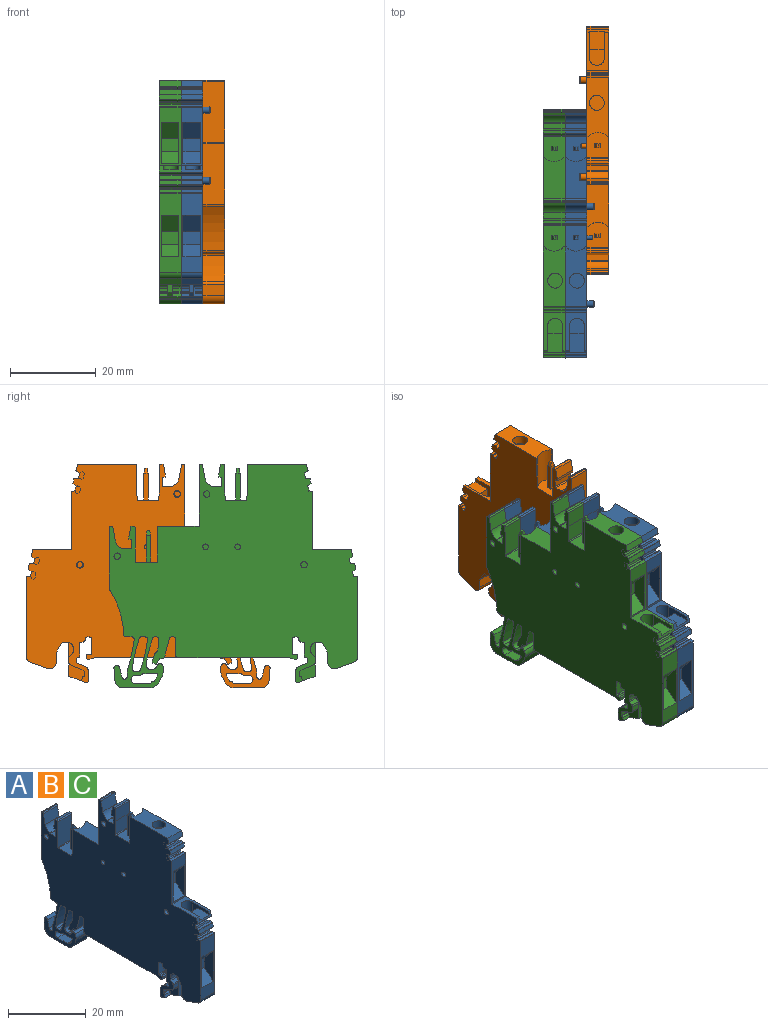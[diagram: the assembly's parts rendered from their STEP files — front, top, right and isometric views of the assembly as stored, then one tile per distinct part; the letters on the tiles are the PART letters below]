
ASSEMBLY  parts=3 mates=3
PART A: 301 faces, bbox 6.8x58x52.3 mm
  f0: cylinder r=0.8mm len=1.6mm, axis (-1,0,0), area 7.6mm2, adj f1,f34
  f1: cone r=0.8mm half-angle=30deg, axis (-1,0,0), area 1.1mm2, adj f0,f287
  f2: plane 1.49x1.49mm, normal (-1,0,0), area 1.7mm2, adj f277
  f3: plane 4.3x0.22mm, normal (0,1,0.02), area 0.8mm2, adj f6,f7,f35,f279
  f4: plane 4.1x0.3mm, normal (0,1,0), area 1.2mm2, adj f5,f34,f56,f279
  f5: plane 4.3x0.3mm, normal (0,1,0.02), area 1.2mm2, adj f4,f7,f34,f279
  f6: plane 4.1x0.22mm, normal (0,1,0), area 0.9mm2, adj f3,f35,f56,f279
  f7: plane 5.93x5.08mm, normal (0,0,1), area 27mm2, adj f3,f5,f34,f35,f229,f258,f259,f260
  f8: cylinder r=1.74mm len=3.48mm, axis (0,0,1), area 23.5mm2, adj f9,f33
  f9: plane 13.79x5.08mm, normal (0,0,1), area 57.6mm2, adj f8,f10,f12,f34,f35,f278,f290
  f10: plane 5.08x1.54mm, normal (0,-0.97,0.24), area 8.1mm2, adj f9,f34,f35,f113
  f11: plane 5.93x5.08mm, normal (0,0,1), area 27mm2, adj f13,f14,f34,f35,f249,f250,f251,f252
  f12: plane 4.1x0.22mm, normal (0,1,0), area 0.9mm2, adj f9,f13,f35,f278
  f13: plane 4.3x0.22mm, normal (0,1,0.02), area 0.8mm2, adj f11,f12,f35,f278
  f14: cylinder r=0.2mm len=5.08mm, axis (1,0,0), area 1.6mm2, adj f11,f15,f34,f35
  f15: plane 5.08x4.1mm, normal (0,-1,0.02), area 20.8mm2, adj f14,f16,f34,f35
  f16: plane 5.08x3.8mm, normal (0,-1,0), area 19.3mm2, adj f15,f17,f34,f35
  f17: cylinder r=0.3mm len=5.08mm, axis (1,0,0), area 2.4mm2, adj f16,f18,f34,f35
  f18: plane 5.08x0.68mm, normal (0,0,1), area 3.5mm2, adj f17,f19,f34,f35
  f19: plane 5.08x2.5mm, normal (0,0.98,0.17), area 12.9mm2, adj f18,f20,f34,f35
  f20: plane 5.08x0.6mm, normal (0,1,0), area 3mm2, adj f19,f21,f34,f35
  f21: plane 5.08x0.67mm, normal (0,0,-1), area 3.4mm2, adj f20,f22,f34,f35
  f22: plane 5.08x1.95mm, normal (0,1,0), area 9.9mm2, adj f21,f23,f34,f35
  f23: cylinder r=0.25mm len=5.08mm, axis (1,0,0), area 2mm2, adj f22,f24,f34,f35
  f24: plane 5.08x1.72mm, normal (0,0,1), area 8.8mm2, adj f23,f25,f34,f35
  f25: cylinder r=0.5mm len=5.08mm, axis (1,0,0), area 0.8mm2, adj f24,f26,f34,f35
  f26: cylinder r=2.57mm len=5.08mm, axis (1,0,0), area 13.5mm2, adj f25,f27,f34,f35
  f27: plane 5.08x3.17mm, normal (0,-0.98,0.18), area 16.3mm2, adj f26,f28,f34,f35
  f28: cylinder r=0.3mm len=5.08mm, axis (1,0,0), area 2.1mm2, adj f27,f29,f34,f35
  f29: plane 5.08x0.24mm, normal (0,0,1), area 1.2mm2, adj f28,f30,f34,f35
  f30: cylinder r=0.3mm len=5.08mm, axis (1,0,0), area 2.4mm2, adj f29,f34,f35,f55
  f31: cylinder r=1.74mm len=3.9mm, axis (0,0,1), area 21.3mm2, adj f32,f65,f66,f68
  f32: plane 6.13x3.9mm, normal (1,0,0), area 11.5mm2, adj f31,f64,f65,f67,f68,f90
  f33: plane 3.48x3.48mm, normal (0,0,1), area 9.5mm2, adj f8
  f34: plane 58x52.25mm, normal (1,0,0), area 1913mm2, adj f0,f4,f5,f7,f9,f10,f11,f14
  f35: plane 58x52.25mm, normal (-1,0,0), area 1919.5mm2, adj f3,f6,f7,f9,f10,f11,f12,f13
  f36: cylinder r=0.5mm len=5.08mm, axis (1,0,0), area 3mm2, adj f34,f35,f37,f43
  f37: cylinder r=35mm len=7.13mm, axis (1,0,0), area 37.2mm2, adj f34,f35,f36,f38
  f38: cylinder r=0.5mm len=5.08mm, axis (1,0,0), area 4.3mm2, adj f34,f35,f37,f39
  f39: plane 5.08x0.99mm, normal (0,0,1), area 5mm2, adj f34,f35,f38,f40
  f40: cylinder r=0.5mm len=5.08mm, axis (1,0,0), area 3.2mm2, adj f34,f35,f39,f41
  f41: cylinder r=35mm len=7.1mm, axis (1,0,0), area 37mm2, adj f34,f35,f40,f42
  f42: cylinder r=0.5mm len=5.08mm, axis (1,0,0), area 4.3mm2, adj f34,f35,f41,f43
  f43: plane 5.08x0.97mm, normal (0,0,-1), area 4.9mm2, adj f34,f35,f36,f42
  f44: plane 5.08x3.02mm, normal (0,0,-1), area 15.4mm2, adj f34,f35,f45,f54
  f45: cylinder r=0.5mm len=5.08mm, axis (1,0,0), area 1.7mm2, adj f34,f35,f44,f46
  f46: cylinder r=1.5mm len=5.08mm, axis (1,0,0), area 5.1mm2, adj f34,f35,f45,f47
  f47: plane 5.08x0.83mm, normal (0,0,-1), area 4.2mm2, adj f34,f35,f46,f48
  f48: cylinder r=0.95mm len=5.08mm, axis (1,0,0), area 15.2mm2, adj f34,f35,f47,f49
  f49: plane 5.08x3.47mm, normal (0,0,1), area 17.6mm2, adj f34,f35,f48,f50
  f50: cylinder r=0.25mm len=5.08mm, axis (1,0,0), area 1.5mm2, adj f34,f35,f49,f51
  f51: cylinder r=0.65mm len=5.08mm, axis (1,0,0), area 4.2mm2, adj f34,f35,f50,f52
  f52: cylinder r=0.25mm len=5.08mm, axis (1,0,0), area 1.4mm2, adj f34,f35,f51,f53
  f53: cylinder r=8.5mm len=5.08mm, axis (1,0,0), area 7.6mm2, adj f34,f35,f52,f54
  f54: cylinder r=0.25mm len=5.08mm, axis (1,0,0), area 2.5mm2, adj f34,f35,f44,f53
  f55: plane 14.2x5.08mm, normal (0,1,0), area 72.1mm2, adj f30,f34,f35,f56
  f56: plane 9.68x5.08mm, normal (0,0,1), area 46.2mm2, adj f4,f6,f34,f35,f55,f279
  f57: plane 1.84x1.31mm, normal (1,0,0), area 1.7mm2, adj f58,f93,f94,f95,f96,f97,f98,f99
  f58: plane 1.24x0.31mm, normal (0,-0.97,0.24), area 0.2mm2, adj f35,f57,f93,f99
  f59: plane 1.24x0.31mm, normal (0,-0.97,0.24), area 0.2mm2, adj f35,f63,f81,f87
  f60: plane 1.73x1.41mm, normal (1,0,0), area 1.7mm2, adj f61,f105,f106,f107,f108,f109,f110,f111
  f61: plane 1.24x0.31mm, normal (0,-0.97,0.24), area 0.2mm2, adj f35,f60,f105,f111
  f62: plane 2.91x1.06mm, normal (0,-0.34,-0.94), area 3.1mm2, adj f136,f235,f236,f237
  f63: plane 1.73x1.41mm, normal (1,0,0), area 1.7mm2, adj f59,f81,f82,f83,f84,f85,f86,f87
  f64: plane 4.23x3.48mm, normal (0,0,1), area 14.7mm2, adj f32,f66,f67,f90
  f65: plane 3.64x3.48mm, normal (0,0,1), area 11.4mm2, adj f31,f32,f66,f67
  f66: plane 6.13x3.9mm, normal (-1,0,0), area 11.5mm2, adj f31,f64,f65,f67,f68,f90
  f67: plane 3.48x2.9mm, normal (0,1,0), area 10.1mm2, adj f32,f64,f65,f66
  f68: plane 8.9x5.08mm, normal (0,0,1), area 20mm2, adj f31,f32,f34,f35,f66,f90,f91
  f69: plane 5.08x0.19mm, normal (0,0.24,0.97), area 1mm2, adj f34,f35,f71,f114,f299,f300
  f70: plane 5.08x0.92mm, normal (0,-0.24,-0.97), area 4.7mm2, adj f34,f35,f75,f76,f299,f300
  f71: plane 4.96x0.52mm, normal (0,0.86,0.51), area 3mm2, adj f34,f69,f72,f299
  f72: plane 4.96x0.32mm, normal (0,0.24,0.97), area 1.6mm2, adj f34,f71,f73,f299
  f73: plane 4.96x0.36mm, normal (0,-0.51,0.86), area 2.1mm2, adj f34,f72,f74,f299
  f74: plane 4.96x1.07mm, normal (0,-0.97,0.24), area 5.5mm2, adj f34,f73,f75,f299
  f75: plane 4.96x0.36mm, normal (0,-0.86,-0.51), area 2.1mm2, adj f34,f70,f74,f299
  f76: plane 5.08x0.65mm, normal (0,-0.53,-0.85), area 3.9mm2, adj f34,f35,f70,f77
  f77: cylinder r=0.1mm len=5.08mm, axis (1,0,0), area 0.6mm2, adj f34,f35,f76,f78
  f78: plane 5.08x1.1mm, normal (0,-0.97,0.24), area 5.8mm2, adj f34,f35,f77,f79
  f79: cylinder r=0.1mm len=5.08mm, axis (1,0,0), area 0.6mm2, adj f34,f35,f78,f80
  f80: plane 5.08x0.77mm, normal (0,-0.07,1), area 3.9mm2, adj f34,f35,f79,f81
  f81: plane 5.08x0.92mm, normal (0,0.24,0.97), area 4.7mm2, adj f34,f35,f59,f63,f80,f82
  f82: plane 4.96x0.36mm, normal (0,-0.51,0.86), area 2.1mm2, adj f34,f63,f81,f83
  f83: plane 4.96x1.07mm, normal (0,-0.97,0.24), area 5.5mm2, adj f34,f63,f82,f84
  f84: plane 4.96x0.36mm, normal (0,-0.86,-0.52), area 2.1mm2, adj f34,f63,f83,f85
  f85: plane 4.96x0.32mm, normal (0,-0.24,-0.97), area 1.6mm2, adj f34,f63,f84,f86
  f86: plane 4.96x0.52mm, normal (0,0.52,-0.86), area 3mm2, adj f34,f63,f85,f87
  f87: plane 5.08x0.19mm, normal (0,-0.24,-0.97), area 1mm2, adj f34,f35,f59,f63,f86,f88
  f88: plane 5.08x0.65mm, normal (0,-0.53,-0.85), area 3.9mm2, adj f34,f35,f87,f89
  f89: cylinder r=0.1mm len=5.08mm, axis (1,0,0), area 0.6mm2, adj f34,f35,f88,f90
  f90: plane 5.08x1.54mm, normal (0,-0.97,0.24), area 4.5mm2, adj f32,f34,f35,f64,f66,f68,f89
  f91: plane 13.62x5.08mm, normal (0,-1,0), area 29.8mm2, adj f34,f35,f68,f92,f238,f242,f244,f245
  f92: plane 5.08x0.79mm, normal (0,-0.07,1), area 4mm2, adj f34,f35,f91,f93
  f93: plane 5.08x0.19mm, normal (0,0.24,0.97), area 1mm2, adj f34,f35,f57,f58,f92,f94
  f94: plane 4.96x0.52mm, normal (0,0.86,0.52), area 3mm2, adj f34,f57,f93,f95
  f95: plane 4.96x0.32mm, normal (0,0.24,0.97), area 1.6mm2, adj f34,f57,f94,f96
  f96: plane 4.96x0.36mm, normal (0,-0.52,0.86), area 2.1mm2, adj f34,f57,f95,f97
  f97: plane 4.96x1.07mm, normal (0,-0.97,0.24), area 5.5mm2, adj f34,f57,f96,f98
  f98: plane 4.96x0.36mm, normal (0,-0.86,-0.52), area 2.1mm2, adj f34,f57,f97,f99
  f99: plane 5.08x0.92mm, normal (0,-0.24,-0.97), area 4.7mm2, adj f34,f35,f57,f58,f98,f100
  f100: plane 5.08x0.65mm, normal (0,-0.53,-0.85), area 3.9mm2, adj f34,f35,f99,f101
  f101: cylinder r=0.1mm len=5.08mm, axis (1,0,0), area 0.6mm2, adj f34,f35,f100,f102
  f102: plane 5.08x1.1mm, normal (0,-0.97,0.24), area 5.8mm2, adj f34,f35,f101,f103
  f103: cylinder r=0.1mm len=5.08mm, axis (1,0,0), area 0.6mm2, adj f34,f35,f102,f104
  f104: plane 5.08x0.77mm, normal (0,-0.07,1), area 3.9mm2, adj f34,f35,f103,f105
  f105: plane 5.08x0.92mm, normal (0,0.24,0.97), area 4.7mm2, adj f34,f35,f60,f61,f104,f106
  f106: plane 4.96x0.36mm, normal (0,-0.52,0.86), area 2.1mm2, adj f34,f60,f105,f107
  f107: plane 4.96x1.07mm, normal (0,-0.97,0.24), area 5.5mm2, adj f34,f60,f106,f108
  f108: plane 4.96x0.36mm, normal (0,-0.86,-0.51), area 2.1mm2, adj f34,f60,f107,f109
  f109: plane 4.96x0.32mm, normal (0,-0.24,-0.97), area 1.6mm2, adj f34,f60,f108,f110
  f110: plane 4.96x0.52mm, normal (0,0.51,-0.86), area 3mm2, adj f34,f60,f109,f111
  f111: plane 5.08x0.19mm, normal (0,-0.24,-0.97), area 1mm2, adj f34,f35,f60,f61,f110,f112
  f112: plane 5.08x0.65mm, normal (0,-0.53,-0.85), area 3.9mm2, adj f34,f35,f111,f113
  f113: cylinder r=0.1mm len=5.08mm, axis (1,0,0), area 0.6mm2, adj f10,f34,f35,f112
  f114: plane 5.08x0.77mm, normal (0,-0.07,1), area 3.9mm2, adj f34,f35,f69,f115
  f115: cylinder r=0.1mm len=5.08mm, axis (1,0,0), area 0.8mm2, adj f34,f35,f114,f230
  f116: cylinder r=1.5mm len=5.08mm, axis (1,0,0), area 9.3mm2, adj f34,f35,f117,f230
  f117: plane 5.08x4mm, normal (0,-0.34,-0.94), area 21.6mm2, adj f34,f35,f116,f118
  f118: cylinder r=1.5mm len=5.08mm, axis (1,0,0), area 14.6mm2, adj f34,f35,f117,f119
  f119: plane 5.08x2.16mm, normal (0,1,0), area 11mm2, adj f34,f35,f118,f120
  f120: cylinder r=0.5mm len=5.08mm, axis (1,0,0), area 1.3mm2, adj f34,f35,f119,f121
  f121: plane 5.08x1.85mm, normal (0,0.87,-0.5), area 10.9mm2, adj f34,f35,f120,f122
  f122: cylinder r=1mm len=5.08mm, axis (1,0,0), area 5.3mm2, adj f34,f35,f121,f123
  f123: plane 5.08x0.5mm, normal (0,0,-1), area 2.5mm2, adj f34,f35,f122,f124
  f124: cylinder r=1.5mm len=5.08mm, axis (1,0,0), area 10.1mm2, adj f34,f35,f123,f125,f231,f235,f236,f237
  f125: plane 2.08x0.71mm, normal (0,-1,0), area 1.5mm2, adj f34,f124,f126,f235
  f126: cylinder r=0.5mm len=2.08mm, axis (1,0,0), area 0.8mm2, adj f34,f125,f127,f235
  f127: plane 2.08x0.71mm, normal (0,-0.71,0.71), area 2.1mm2, adj f34,f126,f128,f235
  f128: cylinder r=0.5mm len=2.08mm, axis (1,0,0), area 0.8mm2, adj f34,f127,f129,f235
  f129: plane 2.08x1.24mm, normal (0,-1,0), area 2.6mm2, adj f34,f128,f130,f235
  f130: cylinder r=0.5mm len=2.08mm, axis (1,0,0), area 1.2mm2, adj f34,f129,f131,f235
  f131: plane 2.97x2.08mm, normal (0,-0.37,-0.93), area 6.7mm2, adj f34,f130,f132,f235
  f132: cylinder r=0.5mm len=2.08mm, axis (1,0,0), area 1.2mm2, adj f34,f131,f133,f235
  f133: plane 2.08x0.77mm, normal (0,-1,0), area 1.6mm2, adj f34,f132,f134,f235
  f134: cylinder r=0.2mm len=2.08mm, axis (1,0,0), area 0.4mm2, adj f34,f133,f135,f235
  f135: cylinder r=0.75mm len=2.08mm, axis (1,0,0), area 1.1mm2, adj f34,f134,f136,f235
  f136: plane 5.08x0.7mm, normal (0,-0.94,0.34), area 3.1mm2, adj f34,f35,f62,f135,f137,f235,f236,f298
  f137: plane 5.08x1.04mm, normal (0,-0.34,-0.94), area 5.6mm2, adj f34,f35,f136,f138
  f138: cylinder r=0.5mm len=5.08mm, axis (1,0,0), area 4.9mm2, adj f34,f35,f137,f139
  f139: plane 5.08x1.97mm, normal (0,1,0), area 10mm2, adj f34,f35,f138,f140
  f140: cylinder r=1.5mm len=5.08mm, axis (1,0,0), area 9.1mm2, adj f34,f35,f139,f141
  f141: plane 5.08x1.87mm, normal (0,0.37,0.93), area 10.2mm2, adj f34,f35,f140,f142
  f142: cylinder r=0.2mm len=5.08mm, axis (1,0,0), area 0.7mm2, adj f34,f35,f141,f143
  f143: plane 5.08x0.8mm, normal (0,1,0), area 4.1mm2, adj f34,f35,f142,f144
  f144: cylinder r=0.25mm len=5.08mm, axis (1,0,0), area 1.9mm2, adj f34,f35,f143,f145
  f145: plane 5.08x0.38mm, normal (0,0.06,-1), area 1.9mm2, adj f34,f35,f144,f146
  f146: cylinder r=0.2mm len=5.08mm, axis (1,0,0), area 1.5mm2, adj f34,f35,f145,f147
  f147: plane 5.08x3.28mm, normal (0,1,0), area 16.6mm2, adj f34,f35,f146,f148
  f148: cylinder r=0.2mm len=5.08mm, axis (1,0,0), area 1.6mm2, adj f34,f35,f147,f149
  f149: plane 5.08x0.6mm, normal (0,0,-1), area 3mm2, adj f34,f35,f148,f150
  f150: cylinder r=0.5mm len=5.08mm, axis (1,0,0), area 4mm2, adj f34,f35,f149,f151
  f151: plane 5.08x0.2mm, normal (0,1,0), area 1mm2, adj f34,f35,f150,f152
  f152: cylinder r=0.5mm len=5.08mm, axis (1,0,0), area 4mm2, adj f34,f35,f151,f153
  f153: plane 5.08x0.45mm, normal (0,0,-1), area 2.3mm2, adj f34,f35,f152,f154
  f154: cylinder r=0.5mm len=5.08mm, axis (1,0,0), area 4mm2, adj f34,f35,f153,f155
  f155: plane 5.08x3.36mm, normal (0,-1,0), area 17.1mm2, adj f34,f35,f154,f156
  f156: cylinder r=0.25mm len=5.08mm, axis (1,0,0), area 1.7mm2, adj f34,f35,f155,f157
  f157: plane 5.08x0.18mm, normal (0,-0.26,0.97), area 0.9mm2, adj f34,f35,f156,f158
  f158: cylinder r=1mm len=5.08mm, axis (1,0,0), area 2.9mm2, adj f34,f35,f157,f159
  f159: cylinder r=0.25mm len=5.08mm, axis (1,0,0), area 2.4mm2, adj f34,f35,f158,f160
  f160: plane 5.08x0.52mm, normal (0,-1,0), area 2.6mm2, adj f34,f35,f159,f161
  f161: cylinder r=0.25mm len=5.08mm, axis (1,0,0), area 1.7mm2, adj f34,f35,f160,f162
  f162: plane 5.08x0.18mm, normal (0,-0.26,-0.97), area 0.9mm2, adj f34,f35,f161,f163
  f163: cylinder r=1mm len=5.08mm, axis (1,0,0), area 2.7mm2, adj f34,f35,f162,f164
  f164: plane 5.08x1.11mm, normal (0,0.26,-0.97), area 5.8mm2, adj f34,f35,f163,f165
  f165: cylinder r=1mm len=5.08mm, axis (1,0,0), area 1.3mm2, adj f34,f35,f164,f166
  f166: plane 25.75x5.08mm, normal (0,0,-1), area 130.8mm2, adj f34,f35,f165,f167
  f167: cylinder r=0.5mm len=5.08mm, axis (1,0,0), area 4mm2, adj f34,f35,f166,f168
  f168: plane 5.08x3.85mm, normal (0,1,0), area 19.6mm2, adj f34,f35,f167,f169
  f169: cylinder r=0.5mm len=5.08mm, axis (1,0,0), area 4mm2, adj f34,f35,f168,f170
  f170: plane 5.08x0.52mm, normal (0,0,-1), area 2.6mm2, adj f34,f35,f169,f171
  f171: cylinder r=0.5mm len=5.08mm, axis (1,0,0), area 3.3mm2, adj f34,f35,f170,f172
  f172: plane 5.08x4.32mm, normal (0,-0.97,-0.25), area 22.7mm2, adj f34,f35,f171,f173
  f173: cylinder r=0.5mm len=5.08mm, axis (1,0,0), area 3.3mm2, adj f34,f35,f172,f174
  f174: plane 5.08x0.58mm, normal (0,0,-1), area 2.9mm2, adj f34,f35,f173,f175
  f175: cylinder r=0.2mm len=5.08mm, axis (1,0,0), area 1.1mm2, adj f34,f35,f174,f176
  f176: plane 5.08x1.07mm, normal (0,-0.87,-0.5), area 6.3mm2, adj f34,f35,f175,f177
  f177: cylinder r=0.25mm len=5.08mm, axis (1,0,0), area 1.9mm2, adj f34,f35,f176,f178
  f178: plane 5.08x0.53mm, normal (0,0.34,-0.94), area 2.9mm2, adj f34,f35,f177,f179
  f179: cylinder r=0.25mm len=5.08mm, axis (1,0,0), area 1.9mm2, adj f34,f35,f178,f180
  f180: plane 5.08x1.82mm, normal (0,0.97,0.26), area 9.6mm2, adj f34,f35,f179,f181
  f181: cylinder r=0.5mm len=5.08mm, axis (1,0,0), area 2.5mm2, adj f34,f35,f180,f182
  f182: cylinder r=0.5mm len=5.08mm, axis (1,0,0), area 2.6mm2, adj f34,f35,f181,f183
  f183: plane 5.08x1.39mm, normal (0,0.97,0.25), area 7.3mm2, adj f34,f35,f182,f184
  f184: plane 5.08x1.43mm, normal (0,1,0), area 7.3mm2, adj f34,f35,f183,f185
  f185: cylinder r=0.5mm len=5.08mm, axis (1,0,0), area 4mm2, adj f34,f35,f184,f186
  f186: plane 5.08x0.5mm, normal (0,0,-1), area 2.5mm2, adj f34,f35,f185,f187
  f187: cylinder r=0.5mm len=5.08mm, axis (1,0,0), area 3.4mm2, adj f34,f35,f186,f188
  f188: cylinder r=35mm len=6.04mm, axis (1,0,0), area 31.6mm2, adj f34,f35,f187,f189
  f189: cylinder r=1mm len=5.08mm, axis (1,0,0), area 8.7mm2, adj f34,f35,f188,f190
  f190: plane 5.08x0.5mm, normal (0,0,1), area 2.5mm2, adj f34,f35,f189,f191
  f191: cylinder r=1mm len=5.08mm, axis (1,0,0), area 5.2mm2, adj f34,f35,f190,f192
  f192: cylinder r=1mm len=5.08mm, axis (1,0,0), area 0.2mm2, adj f34,f35,f191,f193
  f193: plane 5.08x0.5mm, normal (0,0.88,0.48), area 2.9mm2, adj f34,f35,f192,f194
  f194: cylinder r=0.65mm len=5.08mm, axis (1,0,0), area 6.9mm2, adj f34,f35,f193,f195
  f195: cylinder r=2.25mm len=5.08mm, axis (1,0,0), area 7.3mm2, adj f34,f35,f194,f196
  f196: cylinder r=2.25mm len=5.08mm, axis (1,0,0), area 2.3mm2, adj f34,f35,f195,f197
  f197: cylinder r=9.5mm len=5.08mm, axis (1,0,0), area 13.5mm2, adj f34,f35,f196,f198
  f198: cylinder r=2.5mm len=5.08mm, axis (1,0,0), area 12.7mm2, adj f34,f35,f197,f199
  f199: plane 6.12x5.08mm, normal (0,0,-1), area 31.1mm2, adj f34,f35,f198,f200
  f200: cylinder r=2mm len=5.08mm, axis (1,0,0), area 15.3mm2, adj f34,f35,f199,f201
  f201: plane 5.08x2.72mm, normal (0,1,-0.07), area 13.9mm2, adj f34,f35,f200,f202
  f202: cylinder r=0.65mm len=5.08mm, axis (1,0,0), area 9.7mm2, adj f34,f35,f201,f203
  f203: plane 5.08x2.3mm, normal (0,-0.97,0.26), area 12.1mm2, adj f34,f35,f202,f204
  f204: cylinder r=0.6mm len=5.08mm, axis (1,0,0), area 8.8mm2, adj f34,f35,f203,f205
  f205: plane 5.08x1.34mm, normal (0,1,0), area 6.8mm2, adj f34,f35,f204,f206
  f206: cylinder r=0.5mm len=5.08mm, axis (1,0,0), area 0.8mm2, adj f34,f35,f205,f207
  f207: cylinder r=35mm len=7.18mm, axis (1,0,0), area 37.5mm2, adj f34,f35,f206,f208
  f208: cylinder r=0.5mm len=5.08mm, axis (1,0,0), area 4.3mm2, adj f34,f35,f207,f209
  f209: plane 5.08x1.46mm, normal (0,0,-1), area 7.4mm2, adj f34,f35,f208,f210
  f210: cylinder r=0.5mm len=5.08mm, axis (1,0,0), area 3.9mm2, adj f34,f35,f209,f211
  f211: cylinder r=20mm len=10.36mm, axis (1,0,0), area 55.7mm2, adj f34,f35,f210,f212
  f212: cylinder r=1mm len=5.08mm, axis (1,0,0), area 2.9mm2, adj f34,f35,f211,f213
  f213: plane 14.17x5.08mm, normal (0,1,0), area 72mm2, adj f34,f35,f212,f214
  f214: cylinder r=0.3mm len=5.08mm, axis (1,0,0), area 2.4mm2, adj f34,f35,f213,f215
  f215: plane 5.08x0.24mm, normal (0,0,1), area 1.2mm2, adj f34,f35,f214,f216
  f216: cylinder r=0.3mm len=5.08mm, axis (1,0,0), area 2.1mm2, adj f34,f35,f215,f217
  f217: plane 5.08x3.17mm, normal (0,-0.98,0.18), area 16.3mm2, adj f34,f35,f216,f218
  f218: cylinder r=2.57mm len=5.08mm, axis (1,0,0), area 13.5mm2, adj f34,f35,f217,f219
  f219: cylinder r=0.5mm len=5.08mm, axis (1,0,0), area 0.8mm2, adj f34,f35,f218,f220
  f220: plane 5.08x1.72mm, normal (0,0,1), area 8.8mm2, adj f34,f35,f219,f221
  f221: cylinder r=0.25mm len=5.08mm, axis (1,0,0), area 2mm2, adj f34,f35,f220,f222
  f222: plane 5.08x1.95mm, normal (0,1,0), area 9.9mm2, adj f34,f35,f221,f223
  f223: plane 5.08x0.67mm, normal (0,0,-1), area 3.4mm2, adj f34,f35,f222,f224
  f224: plane 5.08x0.6mm, normal (0,1,0), area 3mm2, adj f34,f35,f223,f225
  f225: plane 5.08x2.5mm, normal (0,0.98,0.17), area 12.9mm2, adj f34,f35,f224,f226
  f226: plane 5.08x0.68mm, normal (0,0,1), area 3.5mm2, adj f34,f35,f225,f227
  f227: cylinder r=0.3mm len=5.08mm, axis (1,0,0), area 2.4mm2, adj f34,f35,f226,f228
  f228: plane 7.9x5.08mm, normal (0,-1,0.01), area 40.2mm2, adj f34,f35,f227,f229
  f229: cylinder r=0.2mm len=5.08mm, axis (1,0,0), area 1.6mm2, adj f7,f34,f35,f228
  f230: plane 18.47x5.08mm, normal (0,-1,0), area 54.5mm2, adj f34,f35,f115,f116,f239,f241,f288,f289
  f231: plane 2x0.71mm, normal (0,-1,0), area 1.4mm2, adj f35,f124,f232,f236
  f232: cylinder r=0.5mm len=2mm, axis (1,0,0), area 0.8mm2, adj f35,f231,f233,f236
  f233: plane 2x0.71mm, normal (0,-0.71,0.71), area 2mm2, adj f35,f232,f234,f236
  f234: cylinder r=0.5mm len=2mm, axis (1,0,0), area 0.8mm2, adj f35,f233,f236,f292
  f235: plane 8.97x3.63mm, normal (1,0,0), area 11.8mm2, adj f62,f124,f125,f126,f127,f128,f129,f130
  f236: plane 8.97x3.63mm, normal (-1,0,0), area 11.8mm2, adj f62,f124,f136,f231,f232,f233,f234,f237
  f237: plane 7.91x1mm, normal (0,-1,0), area 7.9mm2, adj f62,f124,f235,f236
  f238: plane 4.08x3.9mm, normal (0,-0.77,-0.64), area 20.8mm2, adj f91,f243,f244,f245
  f239: plane 4.08x3.28mm, normal (0,-0.64,0.77), area 17.4mm2, adj f230,f240,f288,f289
  f240: plane 4.08x3mm, normal (0,-1,0), area 12.2mm2, adj f239,f241,f288,f289
  f241: plane 4.08x3.9mm, normal (0,-0.77,-0.64), area 20.8mm2, adj f230,f240,f288,f289
  f242: plane 4.08x3.28mm, normal (0,-0.64,0.77), area 17.4mm2, adj f91,f243,f244,f245
  f243: plane 4.08x3mm, normal (0,-1,0), area 12.2mm2, adj f238,f242,f244,f245
  f244: plane 9.65x3.28mm, normal (1,0,0), area 20.7mm2, adj f91,f238,f242,f243
  f245: plane 9.65x3.28mm, normal (-1,0,0), area 20.7mm2, adj f91,f238,f242,f243
  f246: plane 1.22x1.1mm, normal (0,0.98,0.17), area 0.9mm2, adj f247,f250,f253,f254
  f247: plane 0.61x0.42mm, normal (0,0,1), area 0.3mm2, adj f246,f248,f253,f254
  f248: plane 1.22x1.1mm, normal (0,-0.98,0.17), area 0.9mm2, adj f247,f249,f253,f254
  f249: plane 6.3x1.22mm, normal (0,-1,0), area 7.7mm2, adj f11,f248,f251,f252
  f250: plane 6.3x1.22mm, normal (0,1,0), area 7.7mm2, adj f11,f246,f251,f252
  f251: plane 6.3x1mm, normal (-1,0,0), area 6.3mm2, adj f11,f249,f250,f254
  f252: plane 6.3x1mm, normal (1,0,0), area 6.3mm2, adj f11,f249,f250,f253
  f253: plane 1.1x1mm, normal (0.94,0,0.34), area 0.9mm2, adj f246,f247,f248,f252
  f254: plane 1.1x1mm, normal (-0.94,0,0.34), area 0.9mm2, adj f246,f247,f248,f251
  f255: plane 1.22x1.1mm, normal (0,0.98,0.17), area 0.9mm2, adj f256,f259,f262,f263
  f256: plane 0.61x0.42mm, normal (0,0,1), area 0.3mm2, adj f255,f257,f262,f263
  f257: plane 1.22x1.1mm, normal (0,-0.98,0.17), area 0.9mm2, adj f256,f258,f262,f263
  f258: plane 6.3x1.22mm, normal (0,-1,0), area 7.7mm2, adj f7,f257,f260,f261
  f259: plane 6.3x1.22mm, normal (0,1,0), area 7.7mm2, adj f7,f255,f260,f261
  f260: plane 6.3x1mm, normal (-1,0,0), area 6.3mm2, adj f7,f258,f259,f263
  f261: plane 6.3x1mm, normal (1,0,0), area 6.3mm2, adj f7,f258,f259,f262
  f262: plane 1.1x1mm, normal (0.94,0,0.34), area 0.9mm2, adj f255,f256,f257,f261
  f263: plane 1.1x1mm, normal (-0.94,0,0.34), area 0.9mm2, adj f255,f256,f257,f260
  f264: cylinder r=0.5mm len=1.27mm, axis (-1,0,0), area 4mm2, adj f34,f265
  f265: cone r=0.5mm half-angle=30deg, axis (-1,0,0), area 0.5mm2, adj f264,f266
  f266: plane 0.83x0.83mm, normal (1,0,0), area 0.5mm2, adj f265
  f267: cylinder r=0.5mm len=1.27mm, axis (-1,0,0), area 4mm2, adj f34,f268
  f268: cone r=0.5mm half-angle=30deg, axis (-1,0,0), area 0.5mm2, adj f267,f269
  f269: plane 0.83x0.83mm, normal (1,0,0), area 0.5mm2, adj f268
  f270: cylinder r=0.65mm len=2.5mm, axis (-1,0,0), area 10.2mm2, adj f35,f271
  f271: plane 1.3x1.3mm, normal (-1,0,0), area 1.3mm2, adj f270
  f272: cylinder r=0.65mm len=2.5mm, axis (-1,0,0), area 10.2mm2, adj f35,f273
  f273: plane 1.3x1.3mm, normal (-1,0,0), area 1.3mm2, adj f272
  f274: cylinder r=0.8mm len=1.6mm, axis (-1,0,0), area 7.6mm2, adj f34,f275
  f275: cone r=0.8mm half-angle=30deg, axis (-1,0,0), area 1.1mm2, adj f274,f276
  f276: plane 1.37x1.37mm, normal (1,0,0), area 1.5mm2, adj f275
  f277: cylinder r=0.74mm len=1.9mm, axis (-1,0,0), area 8.9mm2, adj f2,f35
  f278: cylinder r=3.2mm len=8.4mm, axis (0,0,1), area 43mm2, adj f9,f11,f12,f13,f290,f291
  f279: cylinder r=3.2mm len=8.4mm, axis (0,0,-1), area 43mm2, adj f3,f4,f5,f6,f7,f56
  f280: plane 1.49x1.49mm, normal (-1,0,0), area 1.7mm2, adj f281
  f281: cylinder r=0.74mm len=1.9mm, axis (-1,0,0), area 8.9mm2, adj f35,f280
  f282: plane 1.37x1.37mm, normal (1,0,0), area 1.5mm2, adj f283
  f283: cone r=0.8mm half-angle=30deg, axis (-1,0,0), area 1.1mm2, adj f282,f284
  f284: cylinder r=0.8mm len=1.6mm, axis (-1,0,0), area 7.6mm2, adj f34,f283
  f285: plane 1.49x1.49mm, normal (-1,0,0), area 1.7mm2, adj f286
  f286: cylinder r=0.74mm len=1.9mm, axis (-1,0,0), area 8.9mm2, adj f35,f285
  f287: plane 1.37x1.37mm, normal (1,0,0), area 1.5mm2, adj f1
  f288: plane 9.65x3.28mm, normal (-1,0,0), area 20.7mm2, adj f230,f239,f240,f241
  f289: plane 9.65x3.28mm, normal (1,0,0), area 20.7mm2, adj f230,f239,f240,f241
  f290: plane 4.1x0.3mm, normal (0,1,0), area 1.2mm2, adj f9,f34,f278,f291
  f291: plane 4.3x0.3mm, normal (0,1,0.02), area 1.2mm2, adj f11,f34,f278,f290
  f292: plane 2x1.24mm, normal (0,-1,0), area 2.5mm2, adj f35,f234,f236,f293
  f293: cylinder r=0.5mm len=2mm, axis (1,0,0), area 1.2mm2, adj f35,f236,f292,f294
  f294: plane 2.97x2mm, normal (0,-0.37,-0.93), area 6.4mm2, adj f35,f236,f293,f295
  f295: cylinder r=0.5mm len=2mm, axis (1,0,0), area 1.2mm2, adj f35,f236,f294,f296
  f296: plane 2x0.77mm, normal (0,-1,0), area 1.5mm2, adj f35,f236,f295,f297
  f297: cylinder r=0.2mm len=2mm, axis (1,0,0), area 0.4mm2, adj f35,f236,f296,f298
  f298: cylinder r=0.75mm len=2mm, axis (1,0,0), area 1.1mm2, adj f35,f136,f236,f297
  f299: plane 1.84x1.31mm, normal (1,0,0), area 1.7mm2, adj f69,f70,f71,f72,f73,f74,f75,f300
  f300: plane 1.24x0.31mm, normal (0,-0.97,0.24), area 0.2mm2, adj f35,f69,f70,f299
PART B: same geometry as A
PART C: same geometry as A
PLACE A t=(-11.52,-13.94,7.89)mm
PLACE B rot(axis=(0,0,-1),180deg) t=(-1.36,63.49,7.89)mm
PLACE C t=(-16.6,-13.94,7.89)mm fixed
MATE planar B.f34 <-> A.f34  axis (-1,0,0) through (-6.44,35.93,33)mm
MATE fastened C.f274 <-> A.f277  axis (-1,0,0) through (-11.52,-1.37,36.64)mm
MATE planar B.f166 <-> A.f166  axis (0,0,-1) through (-3.9,34.37,14.94)mm
